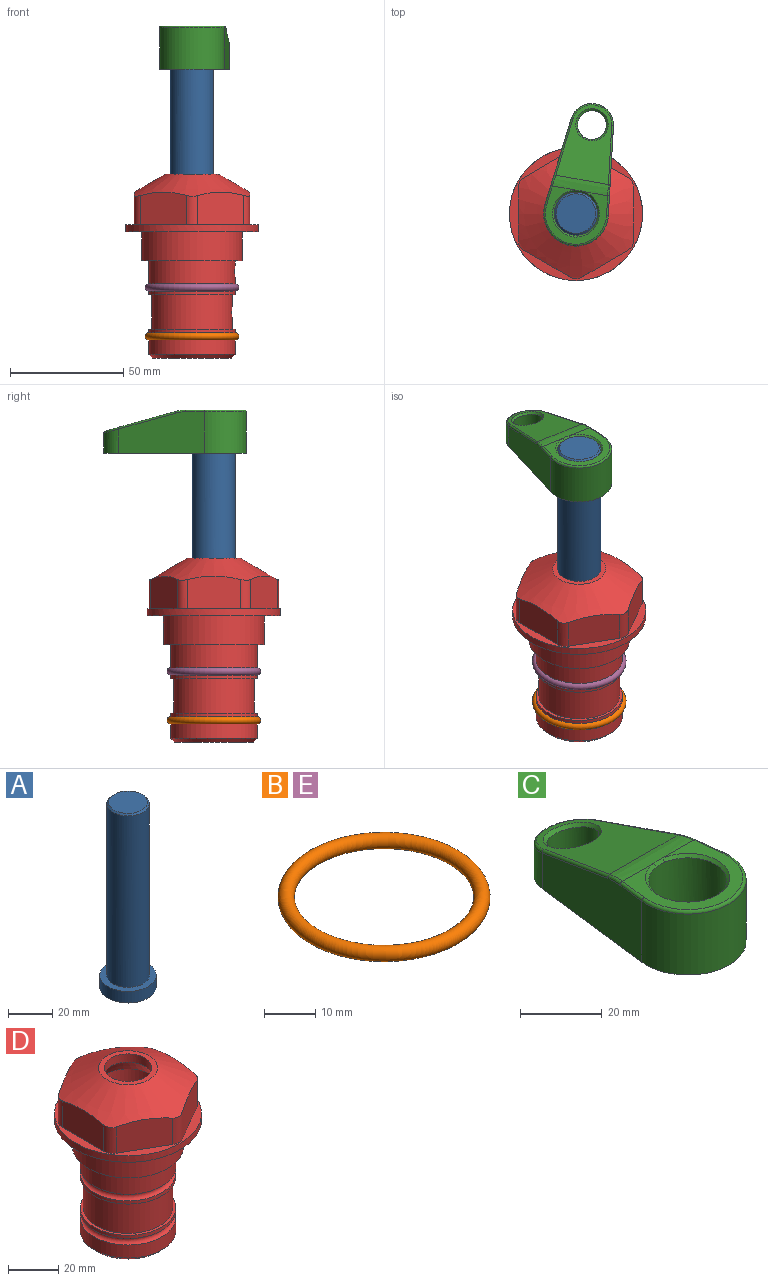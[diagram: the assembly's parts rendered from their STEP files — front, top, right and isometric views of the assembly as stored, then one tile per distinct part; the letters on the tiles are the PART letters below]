
ASSEMBLY  parts=5 mates=4
PART A: 6 faces, bbox 25.4x25.4x101.6 mm
  f0: plane 17.46x17.46mm, normal (0,0,1), area 239.5mm2, adj f5
  f1: plane 25.4x25.4mm, normal (0,0,-1), area 506.7mm2, adj f2
  f2: cylinder r=12.7mm len=25.4mm, axis (0,0,1), area 506.7mm2, adj f1,f3
  f3: plane 25.4x25.4mm, normal (0,0,1), area 221.7mm2, adj f2,f4
  f4: cylinder r=9.53mm len=94.46mm, axis (0,0,1), area 5653mm2, adj f3,f5
  f5: cone r=8.73mm half-angle=45deg, axis (0,0,-1), area 64.4mm2, adj f0,f4
PART B: 1 faces, bbox 44.7x44.7x3.2 mm
  f0: torus R=19.05mm, axis (0,0,1), area 1193.9mm2
PART C: 31 faces, bbox 31.7x65.5x19.8 mm
  f0: plane 39.12x18.26mm, normal (0.99,0.12,0), area 612.2mm2, adj f1,f4,f7,f11,f13,f15
  f1: cylinder r=9.53mm len=18.91mm, axis (0,0,-1), area 296.1mm2, adj f0,f2,f7,f17
  f2: plane 39.12x18.26mm, normal (-0.99,0.12,0), area 612.2mm2, adj f1,f4,f7,f12,f14,f16
  f3: cylinder r=6.35mm len=12.7mm, axis (0,0,-1), area 362.4mm2, adj f7,f18
  f4: cylinder r=14.29mm len=28.58mm, axis (0,0,-1), area 882.2mm2, adj f0,f2,f7,f10
  f5: cylinder r=9.53mm len=19.05mm, axis (0,0,-1), area 1092.6mm2, adj f7,f19,f20
  f6: plane 26.99x23.69mm, normal (0,0,1), area 216.2mm2, adj f9,f10,f11,f12,f19
  f7: plane 63.5x28.58mm, normal (0,0,-1), area 661.8mm2, adj f0,f1,f2,f3,f4,f5,f22,f23
  f8: plane 33.52x23.6mm, normal (0,0.26,0.97), area 486mm2, adj f9,f15,f16,f17,f18
  f9: cylinder r=19.05mm len=24.72mm, axis (1,0,0), area 120.4mm2, adj f6,f8,f13,f14,f20
  f10: torus R=13.49mm, axis (0,0,1), area 59mm2, adj f4,f6,f11,f12
  f11: cylinder r=0.79mm len=8.67mm, axis (0.12,-0.99,0), area 10.8mm2, adj f0,f6,f10,f13
  f12: cylinder r=0.79mm len=8.67mm, axis (0.12,0.99,0), area 10.8mm2, adj f2,f6,f10,f14
  f13: bspline ~4.95x1.42mm, area 6.1mm2, adj f0,f9,f11,f15
  f14: bspline ~4.95x1.42mm, area 6.1mm2, adj f2,f9,f12,f16
  f15: cylinder r=0.79mm len=25.95mm, axis (0.12,-0.96,0.26), area 32.9mm2, adj f0,f8,f13,f17
  f16: cylinder r=0.79mm len=25.95mm, axis (0.12,0.96,-0.26), area 32.9mm2, adj f2,f8,f14,f17
  f17: bspline ~18.91x8.38mm, area 30mm2, adj f1,f8,f15,f16
  f18: bspline ~14.29x14.29mm, area 48.3mm2, adj f3,f8
  f19: cone r=9.53mm half-angle=45deg, axis (0,0,1), area 66.5mm2, adj f5,f6,f20
  f20: bspline ~3.22x0.96mm, area 3.5mm2, adj f5,f9,f19
  f21: plane 2.75x2.72mm, normal (0,0,-1), area 2.9mm2, adj f23,f25,f28
  f22: plane 23.05x15.88mm, normal (-0.99,-0.12,0), area 323.6mm2, adj f7,f25,f26,f27,f28,f29
  f23: plane 23.05x15.88mm, normal (0.99,-0.12,0), area 323.6mm2, adj f7,f21,f25,f27,f28,f30
  f24: cylinder r=9.53mm len=10.69mm, axis (0,0,-1), area 114.7mm2, adj f7,f27,f29,f30
  f25: cylinder r=12.7mm len=20.59mm, axis (0,0,-1), area 381.1mm2, adj f7,f21,f22,f23,f26,f28
  f26: plane 2.75x2.72mm, normal (0,0,-1), area 2.9mm2, adj f22,f25,f28
  f27: plane 19.72x18.37mm, normal (0,-0.26,-0.97), area 291.8mm2, adj f22,f23,f24,f28,f29,f30
  f28: cylinder r=15.88mm len=19.92mm, axis (1,0,0), area 54.8mm2, adj f21,f22,f23,f25,f26,f27
  f29: cylinder r=1.59mm len=11mm, axis (0,0,-1), area 34.7mm2, adj f7,f22,f24,f27
  f30: cylinder r=1.59mm len=11mm, axis (0,0,-1), area 34.7mm2, adj f7,f23,f24,f27
PART D: 36 faces, bbox 58.7x58.7x81 mm
  f0: cylinder r=17.78mm len=35.56mm, axis (0,0,1), area 1670.8mm2, adj f23,f24,f31
  f1: cylinder r=19.05mm len=38.1mm, axis (0,0,1), area 1191.9mm2, adj f26,f27,f30
  f2: plane 58.66x58.66mm, normal (0,0,-1), area 1150.6mm2, adj f3,f28
  f3: cylinder r=29.33mm len=58.66mm, axis (0,0,-1), area 585.1mm2, adj f2,f4
  f4: plane 58.66x58.66mm, normal (0,0,1), area 475.9mm2, adj f3,f5,f6,f7,f8,f9,f10,f11
  f5: plane 20.32x14.34mm, normal (-0.5,0.87,0), area 324.4mm2, adj f4,f15,f16,f17
  f6: plane 20.32x14.34mm, normal (0.5,0.87,0), area 324.4mm2, adj f4,f14,f15,f17
  f7: plane 23.48x14.34mm, normal (1,0,0), area 324.4mm2, adj f4,f13,f14,f17
  f8: plane 20.32x14.34mm, normal (0.5,-0.87,0), area 324.4mm2, adj f4,f12,f13,f17
  f9: plane 20.32x14.34mm, normal (-0.5,-0.87,0), area 324.4mm2, adj f4,f11,f12,f17
  f10: plane 23.48x14.34mm, normal (-1,0,0), area 324.4mm2, adj f4,f11,f16,f17
  f11: cylinder r=5.08mm len=12.85mm, axis (0,0,-1), area 67.2mm2, adj f4,f9,f10,f17
  f12: cylinder r=5.08mm len=12.85mm, axis (0,0,-1), area 67.2mm2, adj f4,f8,f9,f17
  f13: cylinder r=5.08mm len=12.85mm, axis (0,0,-1), area 67.2mm2, adj f4,f7,f8,f17
  f14: cylinder r=5.08mm len=12.85mm, axis (0,0,-1), area 67.2mm2, adj f4,f6,f7,f17
  f15: cylinder r=5.08mm len=12.85mm, axis (0,0,-1), area 67.2mm2, adj f4,f5,f6,f17
  f16: cylinder r=5.08mm len=12.85mm, axis (0,0,-1), area 67.2mm2, adj f4,f5,f10,f17
  f17: cone r=11.73mm half-angle=60deg, axis (0,0,-1), area 2071.8mm2, adj f5,f6,f7,f8,f9,f10,f11,f12
  f18: plane 23.46x23.46mm, normal (0,0,1), area 147.4mm2, adj f17,f35
  f19: plane 34.93x34.93mm, normal (0,0,-1), area 958mm2, adj f29
  f20: cylinder r=19.05mm len=38.1mm, axis (0,0,1), area 760.1mm2, adj f21,f29
  f21: torus R=19.05mm, axis (0,0,1), area 565.3mm2, adj f20,f22
  f22: cylinder r=19.05mm len=38.1mm, axis (0,0,1), area 190mm2, adj f21,f23
  f23: plane 38.1x38.1mm, normal (0,0,1), area 146.9mm2, adj f0,f22
  f24: plane 38.1x38.1mm, normal (0,0,-1), area 146.9mm2, adj f0,f25
  f25: cylinder r=19.05mm len=38.1mm, axis (0,0,1), area 190mm2, adj f24,f26
  f26: torus R=19.05mm, axis (0,0,1), area 565.3mm2, adj f1,f25
  f27: plane 44.45x44.45mm, normal (0,0,-1), area 411.7mm2, adj f1,f28
  f28: cylinder r=22.23mm len=44.45mm, axis (0,0,1), area 1773.5mm2, adj f2,f27
  f29: cone r=19.05mm half-angle=45deg, axis (0,0,1), area 257.5mm2, adj f19,f20
  f30: cylinder r=3.17mm len=6.75mm, axis (-1,0,0), area 128mm2, adj f1,f33
  f31: cylinder r=3.17mm len=6.35mm, axis (-1,0,0), area 102.5mm2, adj f0,f33
  f32: plane 25.4x25.4mm, normal (0,0,1), area 506.7mm2, adj f33
  f33: cylinder r=12.7mm len=66.42mm, axis (0,0,-1), area 5236.2mm2, adj f30,f31,f32,f34
  f34: cone r=9.53mm half-angle=30deg, axis (0,0,-1), area 443.4mm2, adj f33,f35
  f35: cylinder r=9.53mm len=19.05mm, axis (0,0,-1), area 240.9mm2, adj f18,f34
PART E: same geometry as B
PLACE A rot(axis=(0,0,-1),10.2deg) t=(0,0,27.24)mm
PLACE B t=(0,0,-21.59)mm
PLACE C rot(axis=(0,0,-1),10.2deg) t=(0,0,27.24)mm
PLACE D at identity fixed
PLACE E at identity
MATE fastened C.f4 <-> A.f2  axis (0,0,1) through (0,0,90.74)mm
MATE fastened B.f0 <-> D.f0  axis (0,0,1) through (0,0,-46.1)mm
MATE cylindrical A.f2 <-> D.f0  axis (0,0,-1) through (0,0,-10.86)mm
MATE fastened E.f0 <-> D.f0  axis (0,0,1) through (0,0,-24.51)mm
